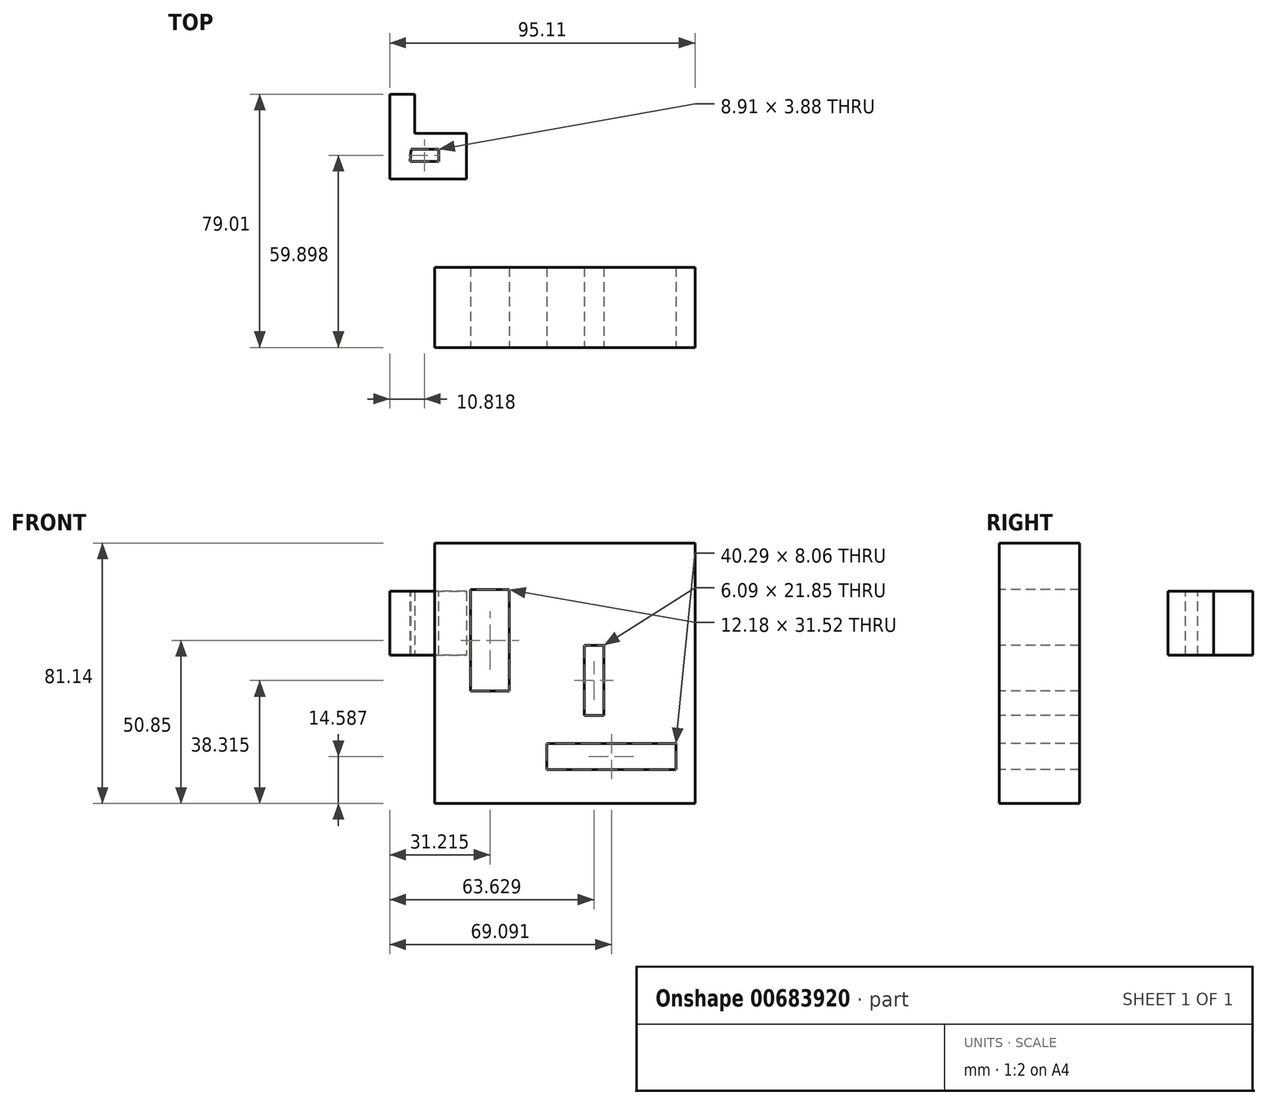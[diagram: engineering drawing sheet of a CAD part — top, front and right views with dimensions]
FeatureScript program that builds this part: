
annotation { "Feature Type Name" : "Feature", "Feature Type Description" : "" }
export const myFeature = defineFeature(function(context is Context, id is Id, definition is map)
    precondition{}
    {
        {
            var Q0;
            Q0=qCreatedBy(makeId("Front.planeOp"),FACE);
            var sketch = newSketch(context, id + "F0", { "sketchPlane" : qUnion([Q0])});
            skLineSegment(sketch, "E0.bottom", {"start": v(-40.39, 34.98) * mm, "end": v(40.75, 34.98) * mm});
            skLineSegment(sketch, "E0.top", {"start": v(-40.39, -46.16) * mm, "end": v(40.75, -46.16) * mm});
            skLineSegment(sketch, "E0.left", {"start": v(-40.39, 34.98) * mm, "end": v(-40.39, -46.16) * mm});
            skLineSegment(sketch, "E0.right", {"start": v(40.75, 34.98) * mm, "end": v(40.75, -46.16) * mm});
            skSolve(sketch);
        }
        {
            var Q0;
            Q0 = qSketchRegion(id + "F0", true);
            extrude(context, id + "F1", {"entities" : qUnion([Q0]), "depth" : 25 * mm, "offsetDistance" : 25 * mm});
        }
        {
            var Q0;
            Q0=makeQuery(id+"F1.opExtrude","CAP_FACE",FACE,{"disambiguationData":[OSD([sQuery(id+"F0.wireOp",EDGE,"E0.bottom"),sQuery(id+"F0.wireOp",EDGE,"E0.top"),sQuery(id+"F0.wireOp",EDGE,"E0.left"),sQuery(id+"F0.wireOp",EDGE,"E0.right")])],"isStart":false});
            var sketch = newSketch(context, id + "F2", { "sketchPlane" : qUnion([Q0])});
            skLineSegment(sketch, "E1.bottom", {"start": v(-29.23, 20.45) * mm, "end": v(-17.06, 20.45) * mm});
            skLineSegment(sketch, "E1.top", {"start": v(-29.23, -11.07) * mm, "end": v(-17.06, -11.07) * mm});
            skLineSegment(sketch, "E1.left", {"start": v(-29.23, 20.45) * mm, "end": v(-29.23, -11.07) * mm});
            skLineSegment(sketch, "E1.right", {"start": v(-17.06, 20.45) * mm, "end": v(-17.06, -11.07) * mm});
            skLineSegment(sketch, "E2.bottom", {"start": v(6.22, 3.08) * mm, "end": v(12.31, 3.08) * mm});
            skLineSegment(sketch, "E2.top", {"start": v(6.22, -18.77) * mm, "end": v(12.31, -18.77) * mm});
            skLineSegment(sketch, "E2.left", {"start": v(6.22, 3.08) * mm, "end": v(6.22, -18.77) * mm});
            skLineSegment(sketch, "E2.right", {"start": v(12.31, 3.08) * mm, "end": v(12.31, -18.77) * mm});
            skLineSegment(sketch, "E3.bottom", {"start": v(-5.42, -27.54) * mm, "end": v(34.88, -27.54) * mm});
            skLineSegment(sketch, "E3.top", {"start": v(-5.42, -35.6) * mm, "end": v(34.88, -35.6) * mm});
            skLineSegment(sketch, "E3.left", {"start": v(-5.42, -27.54) * mm, "end": v(-5.42, -35.6) * mm});
            skLineSegment(sketch, "E3.right", {"start": v(34.88, -27.54) * mm, "end": v(34.88, -35.6) * mm});
            skSolve(sketch);
        }
        {
            var Q0;
            Q0 = qSketchRegion(id + "F2", true);
            extrude(context, id + "F3", {"entities" : qUnion([Q0]), "operationType" : NewBodyOperationType.REMOVE, "endBound" : BoundingType.THROUGH_ALL, "oppositeDirection" : true, "depth" : 25 * mm, "offsetDistance" : 25 * mm});
        }
        {
            var Q0;
            Q0=qCreatedBy(makeId("Top.planeOp"),FACE);
            var sketch = newSketch(context, id + "F4", { "sketchPlane" : qUnion([Q0])});
            skLineSegment(sketch, "E4", {"start": v(-54.36, 54) * mm, "end": v(-54.36, 27.54) * mm});
            skLineSegment(sketch, "E5", {"start": v(-54.36, 27.54) * mm, "end": v(-30.49, 27.54) * mm});
            skLineSegment(sketch, "E6", {"start": v(-30.49, 27.54) * mm, "end": v(-30.49, 41.72) * mm});
            skLineSegment(sketch, "E7", {"start": v(-30.49, 41.72) * mm, "end": v(-46.56, 41.72) * mm});
            skLineSegment(sketch, "E8", {"start": v(-46.56, 41.72) * mm, "end": v(-46.56, 54) * mm});
            skLineSegment(sketch, "E9", {"start": v(-46.56, 54) * mm, "end": v(-54.36, 54) * mm});
            skSolve(sketch);
        }
        {
            var Q0;
            Q0=makeQuery(id+"F4.imprint","IMPRINT",FACE,{"disambiguationData":[TD([[makeQuery(id+"F4.imprint","IMPRINT",EDGE,{"derivedFrom":sQuery(id+"F4.wireOp",EDGE,"E4")}),1.0]])]});
            extrude(context, id + "F5", {"entities" : qUnion([Q0]), "depth" : 20 * mm, "offsetDistance" : 25 * mm});
        }
        {
            var Q0;
            Q0=makeQuery(id+"F5.opExtrude","CAP_FACE",FACE,{"disambiguationData":[OSD([sQuery(id+"F4.wireOp",EDGE,"E4"),sQuery(id+"F4.wireOp",EDGE,"E5"),sQuery(id+"F4.wireOp",EDGE,"E6"),sQuery(id+"F4.wireOp",EDGE,"E7"),sQuery(id+"F4.wireOp",EDGE,"E8"),sQuery(id+"F4.wireOp",EDGE,"E9")])],"isStart":false});
            var sketch = newSketch(context, id + "F6", { "sketchPlane" : qUnion([Q0])});
            skLineSegment(sketch, "E10", {"start": v(-48, 32.96) * mm, "end": v(-39.09, 32.96) * mm});
            skLineSegment(sketch, "E11", {"start": v(-39.09, 32.96) * mm, "end": v(-39.09, 36.84) * mm});
            skLineSegment(sketch, "E12", {"start": v(-39.09, 36.84) * mm, "end": v(-47.7, 36.84) * mm});
            skLineSegment(sketch, "E13", {"start": v(-47.7, 36.84) * mm, "end": v(-48, 32.96) * mm});
            skSolve(sketch);
        }
        {
            var Q0;
            Q0=makeQuery(id+"F6.imprint","IMPRINT",FACE,{"disambiguationData":[TD([[makeQuery(id+"F6.imprint","IMPRINT",EDGE,{"derivedFrom":sQuery(id+"F6.wireOp",EDGE,"E10")}),1.0]])]});
            extrude(context, id + "F7", {"entities" : qUnion([Q0]), "operationType" : NewBodyOperationType.REMOVE, "oppositeDirection" : true, "depth" : 25 * mm, "offsetDistance" : 25 * mm});
        }
    });
